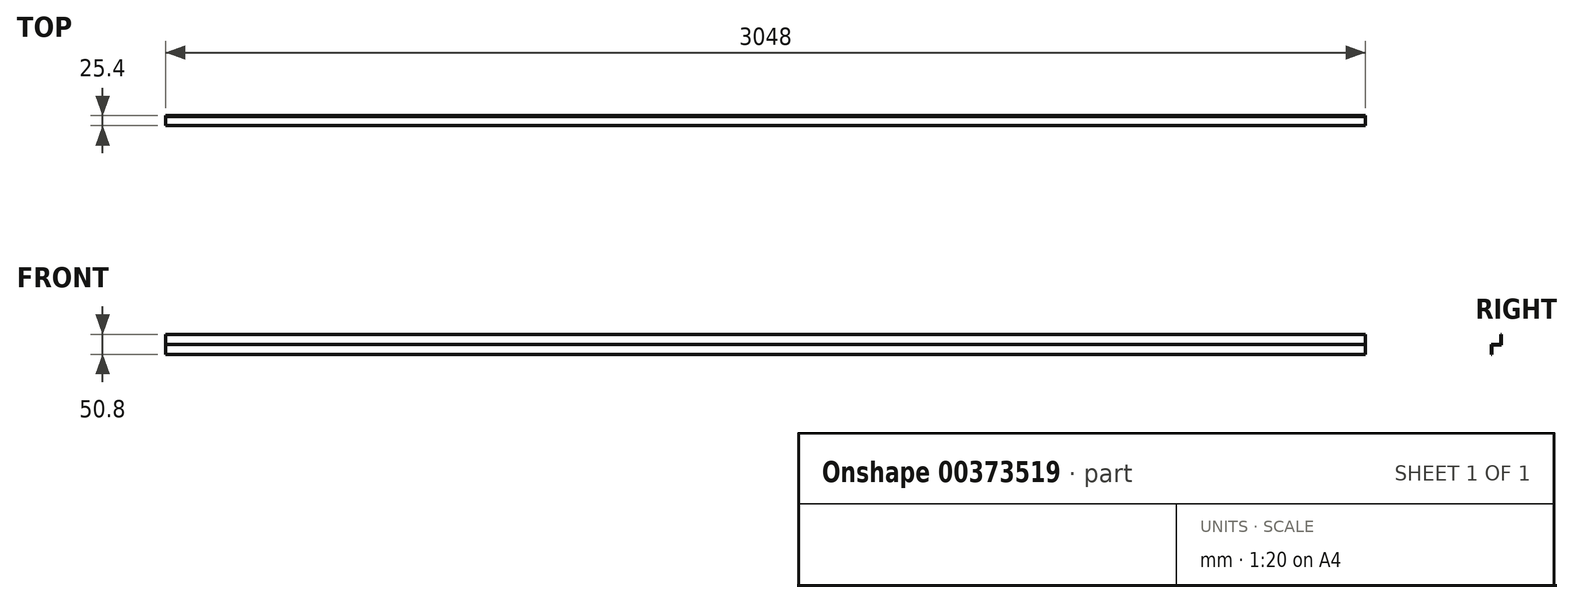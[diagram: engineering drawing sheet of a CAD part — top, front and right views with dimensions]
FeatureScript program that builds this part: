
annotation { "Feature Type Name" : "Feature", "Feature Type Description" : "" }
export const myFeature = defineFeature(function(context is Context, id is Id, definition is map)
    precondition{}
    {
        {
            var Q0;
            Q0=qCreatedBy(makeId("Right.planeOp"),FACE);
            var sketch = newSketch(context, id + "F0", { "sketchPlane" : qUnion([Q0])});
            skLineSegment(sketch, "E0", {"start": v(-12.7, -25.16) * mm, "end": v(-12.7, 0.24) * mm});
            skLineSegment(sketch, "E1", {"start": v(-12.7, 0.24) * mm, "end": v(11.09, 0.24) * mm});
            skLineSegment(sketch, "E2", {"start": v(11.09, 0.24) * mm, "end": v(11.09, 25.64) * mm});
            skLineSegment(sketch, "E3.0", {"start": v(-11.09, -25.16) * mm, "end": v(-11.09, -1.37) * mm});
            skLineSegment(sketch, "E4.0", {"start": v(-11.09, -1.37) * mm, "end": v(12.7, -1.37) * mm});
            skLineSegment(sketch, "E5.0", {"start": v(12.7, 0.24) * mm, "end": v(12.7, 25.64) * mm});
            skLineSegment(sketch, "E6", {"start": v(12.7, -1.37) * mm, "end": v(12.7, -1.37) * mm});
            skLineSegment(sketch, "E7", {"start": v(12.7, -1.37) * mm, "end": v(12.7, 0.24) * mm});
            skLineSegment(sketch, "E8", {"start": v(-11.09, -25.16) * mm, "end": v(-12.7, -25.16) * mm});
            skLineSegment(sketch, "E9", {"start": v(11.09, 25.64) * mm, "end": v(12.7, 25.64) * mm});
            skSolve(sketch);
        }
        {
            var Q0;
            Q0=makeQuery(id+"F0.imprint","IMPRINT",FACE,{"disambiguationData":[TD([[makeQuery(id+"F0.imprint","IMPRINT",EDGE,{"derivedFrom":sQuery(id+"F0.wireOp",EDGE,"E0")}),-1.0]])]});
            extrude(context, id + "F1", {"entities" : qUnion([Q0]), "depth" : 3048 * mm});
        }
    });
